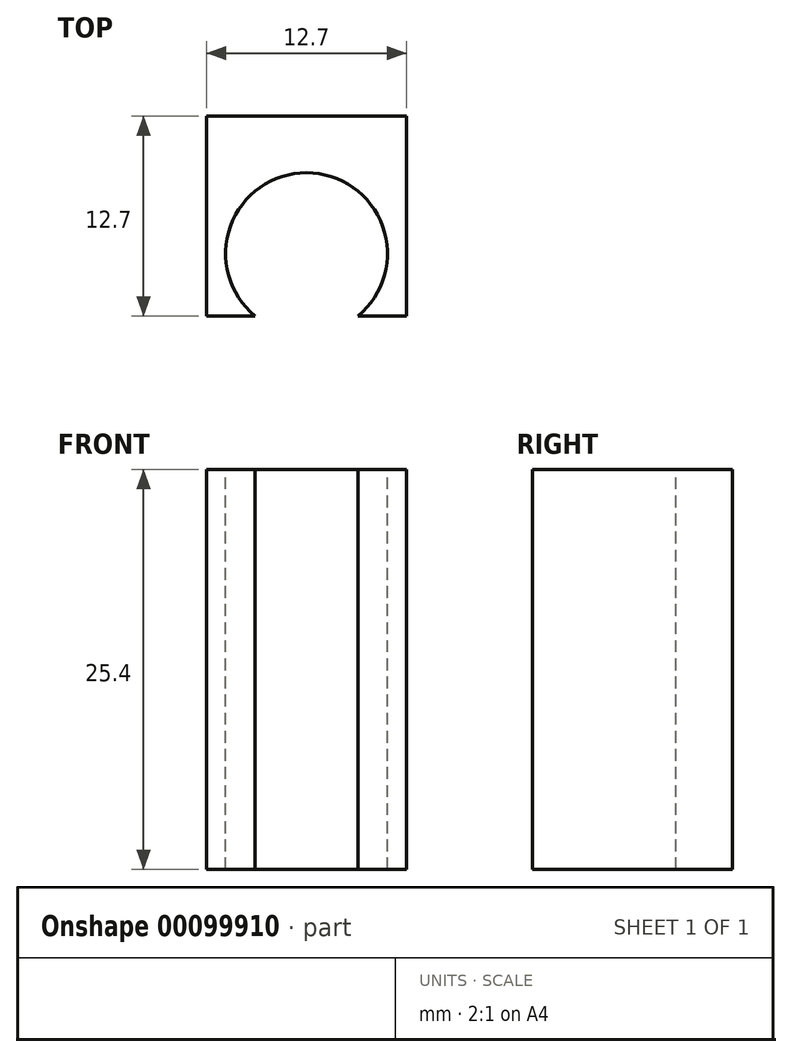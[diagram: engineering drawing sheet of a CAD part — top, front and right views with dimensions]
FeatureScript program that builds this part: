
annotation { "Feature Type Name" : "Feature", "Feature Type Description" : "" }
export const myFeature = defineFeature(function(context is Context, id is Id, definition is map)
    precondition{}
    {
        {
            var Q0;
            Q0=qCreatedBy(makeId("Front.planeOp"),FACE);
            var sketch = newSketch(context, id + "F0", { "sketchPlane" : qUnion([Q0])});
            skLineSegment(sketch, "E0.bottom", {"start": v(0, 0) * mm, "end": v(12.7, 0) * mm});
            skLineSegment(sketch, "E0.top", {"start": v(0, 25.4) * mm, "end": v(12.7, 25.4) * mm});
            skLineSegment(sketch, "E0.left", {"start": v(0, 0) * mm, "end": v(0, 25.4) * mm});
            skLineSegment(sketch, "E0.right", {"start": v(12.7, 0) * mm, "end": v(12.7, 25.4) * mm});
            skSolve(sketch);
        }
        {
            var Q0;
            Q0 = qSketchRegion(id + "F0", true);
            extrude(context, id + "F1", {"entities" : qUnion([Q0]), "depth" : 12.7 * mm});
        }
        {
            var Q0;
            Q0=makeQuery(id+"F1.opExtrude","SWEPT_FACE",FACE,{"disambiguationData":[OSD([sQuery(id+"F0.wireOp",EDGE,"E0.top")])]});
            var sketch = newSketch(context, id + "F2", { "sketchPlane" : qUnion([Q0])});
            skCircle(sketch, "E1", {"center": v(6.35, -8.74) * mm, "radius": 5.14 * mm});
            skPoint(sketch, "E1.centerSnap0", {"position": v(6.35, -12.7) * mm});
            skSolve(sketch);
        }
        {
            var Q0;
            Q0 = qSketchRegion(id + "F2", true);
            extrude(context, id + "F3", {"entities" : qUnion([Q0]), "operationType" : NewBodyOperationType.REMOVE, "endBound" : BoundingType.THROUGH_ALL, "oppositeDirection" : true, "depth" : 25.4 * mm});
        }
    });
